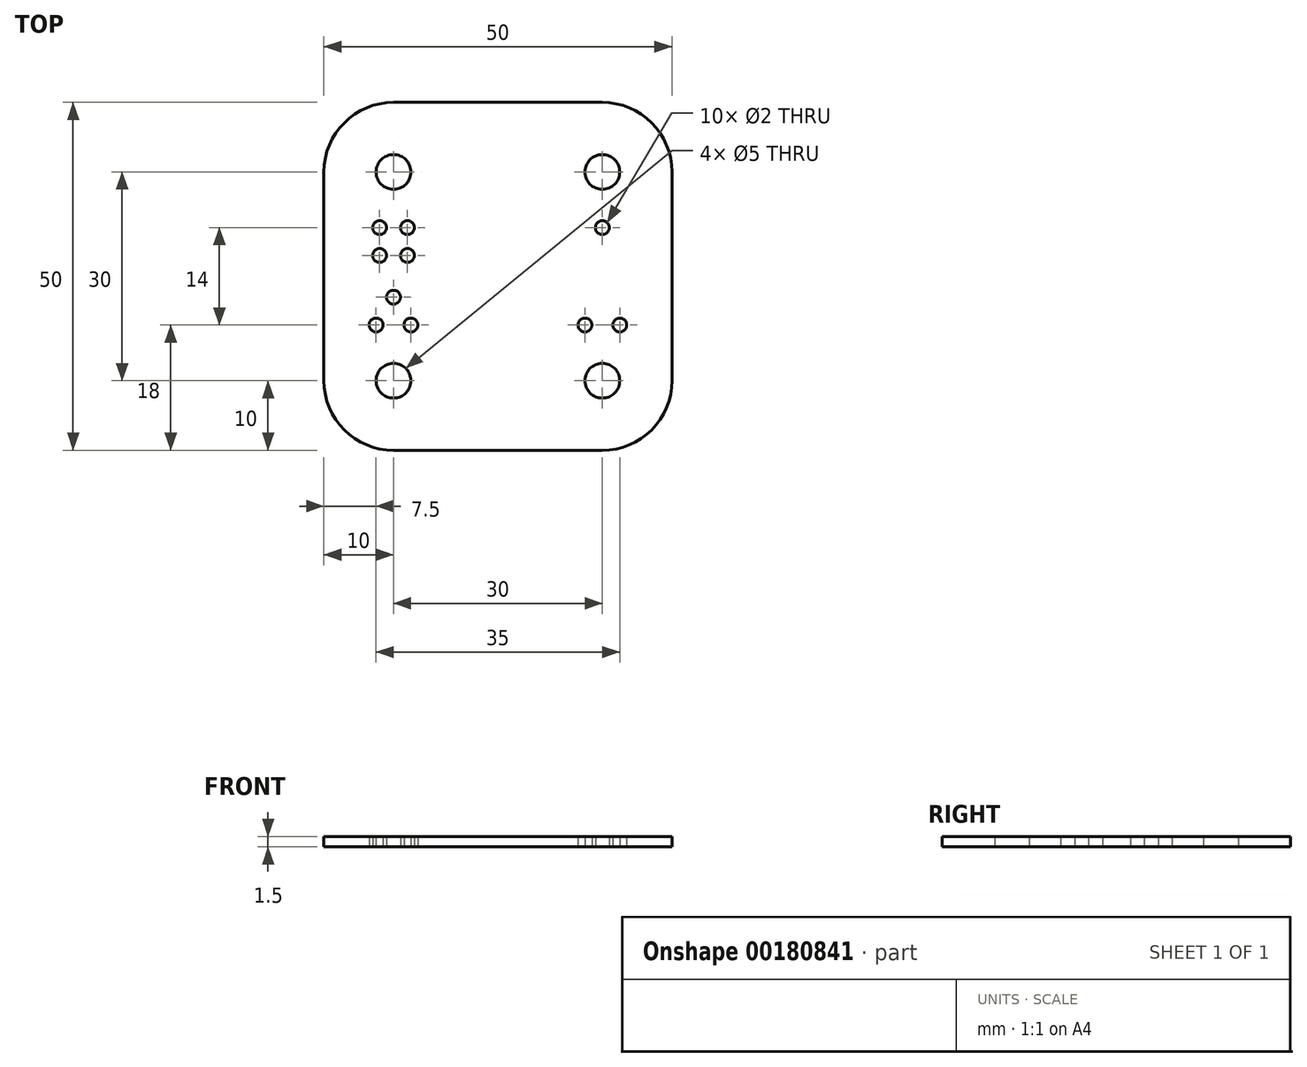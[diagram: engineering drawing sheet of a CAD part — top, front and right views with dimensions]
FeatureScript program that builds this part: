
annotation { "Feature Type Name" : "Feature", "Feature Type Description" : "" }
export const myFeature = defineFeature(function(context is Context, id is Id, definition is map)
    precondition{}
    {
        {
            var Q0;
            Q0=qCreatedBy(makeId("Top.planeOp"),FACE);
            var sketch = newSketch(context, id + "F0", { "sketchPlane" : qUnion([Q0])});
            skLineSegment(sketch, "E0.bottom", {"start": v(10, 0) * mm, "end": v(40, 0) * mm});
            skLineSegment(sketch, "E0.top", {"start": v(10, 50) * mm, "end": v(40, 50) * mm});
            skLineSegment(sketch, "E0.left", {"start": v(0, 10) * mm, "end": v(0, 40) * mm});
            skLineSegment(sketch, "E0.right", {"start": v(50, 10) * mm, "end": v(50, 40) * mm});
            skPoint(sketch, "E1.visualSharp", {"position": v(0, 50) * mm});
            skArc(sketch, "E1.filletArc", {"start": v(10, 50) * mm, "mid": v(2.93, 47.07) * mm, "end": v(0, 40) * mm});
            skPoint(sketch, "E2.visualSharp", {"position": v(50, 50) * mm});
            skArc(sketch, "E2.filletArc", {"start": v(50, 40) * mm, "mid": v(47.07, 47.07) * mm, "end": v(40, 50) * mm});
            skPoint(sketch, "E3.visualSharp", {"position": v(50, 0) * mm});
            skArc(sketch, "E3.filletArc", {"start": v(40, 0) * mm, "mid": v(47.07, 2.93) * mm, "end": v(50, 10) * mm});
            skPoint(sketch, "E4.visualSharp", {"position": v(0, 0) * mm});
            skArc(sketch, "E4.filletArc", {"start": v(0, 10) * mm, "mid": v(2.93, 2.93) * mm, "end": v(10, 0) * mm});
            skCircle(sketch, "E5", {"center": v(10, 40) * mm, "radius": 2.5 * mm});
            skCircle(sketch, "E6", {"center": v(40, 40) * mm, "radius": 2.5 * mm});
            skCircle(sketch, "E7", {"center": v(40, 10) * mm, "radius": 2.5 * mm});
            skCircle(sketch, "E8", {"center": v(10, 10) * mm, "radius": 2.5 * mm});
            skCircle(sketch, "E9", {"center": v(40, 32) * mm, "radius": 1 * mm});
            skCircle(sketch, "E10", {"center": v(42.5, 18) * mm, "radius": 1 * mm});
            skCircle(sketch, "E11", {"center": v(37.5, 18) * mm, "radius": 1 * mm});
            skCircle(sketch, "E12", {"center": v(12.5, 18) * mm, "radius": 1 * mm});
            skCircle(sketch, "E13", {"center": v(7.5, 18) * mm, "radius": 1 * mm});
            skCircle(sketch, "E14", {"center": v(10, 22) * mm, "radius": 1 * mm});
            skCircle(sketch, "E15", {"center": v(8, 28) * mm, "radius": 1 * mm});
            skCircle(sketch, "E16", {"center": v(12, 28) * mm, "radius": 1 * mm});
            skCircle(sketch, "E17", {"center": v(12, 32) * mm, "radius": 1 * mm});
            skCircle(sketch, "E18", {"center": v(8, 32) * mm, "radius": 1 * mm});
            skSolve(sketch);
        }
        {
            var Q0;
            Q0=makeQuery(id+"F0.imprint","IMPRINT",FACE,{"disambiguationData":[TD([[makeQuery(id+"F0.imprint","IMPRINT",EDGE,{"derivedFrom":sQuery(id+"F0.wireOp",EDGE,"E0.bottom")}),1.0]])]});
            extrude(context, id + "F1", {"entities" : qUnion([Q0]), "depth" : 1.5 * mm});
        }
    });
